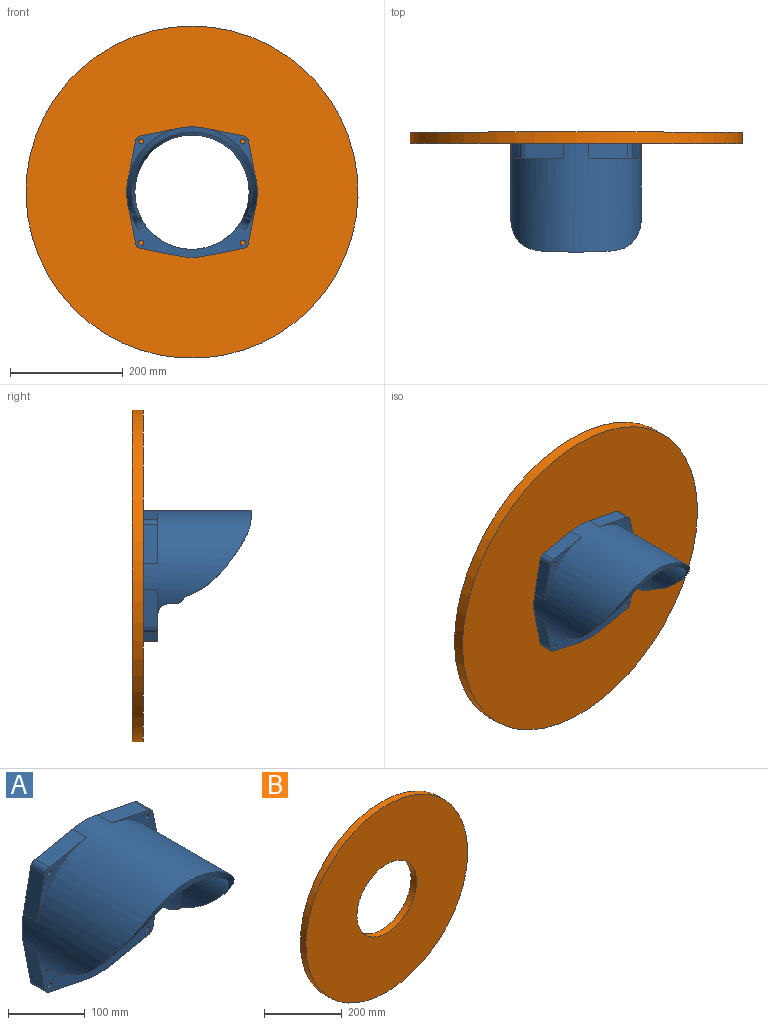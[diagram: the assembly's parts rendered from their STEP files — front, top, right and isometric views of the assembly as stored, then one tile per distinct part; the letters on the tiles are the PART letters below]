
ASSEMBLY  parts=2 mates=1
PART A: 34 faces, bbox 232x193x232 mm
  f0: extruded ~232x154.46mm, area 4830.5mm2, adj f1,f2,f30,f31
  f1: cylinder r=107mm len=214mm, axis (0,1,0), area 37338.6mm2, adj f0,f29,f30,f31
  f2: cylinder r=116mm len=232mm, axis (0,1,0), area 66384.4mm2, adj f0,f3,f4,f5,f11,f12,f14,f15
  f3: plane 90.81x90.81mm, normal (0,-1,0), area 978.9mm2, adj f2,f15,f16,f17,f21
  f4: plane 90.81x90.81mm, normal (0,-1,0), area 978.9mm2, adj f2,f12,f13,f14,f20
  f5: plane 227.43x93.09mm, normal (0,-1,0), area 4952.2mm2, adj f2,f6,f7,f8,f9,f10,f11,f18
  f6: cylinder r=10mm len=26mm, axis (0,1,0), area 305mm2, adj f5,f7,f18,f19
  f7: plane 69.07x26mm, normal (-0.2,0,-0.98), area 1831.8mm2, adj f5,f6,f8,f19
  f8: cylinder r=116mm len=45.81mm, axis (0,1,0), area 1199mm2, adj f5,f7,f9,f19
  f9: plane 69.07x26mm, normal (0.2,0,-0.98), area 1831.8mm2, adj f5,f8,f10,f19
  f10: cylinder r=10mm len=26mm, axis (0,1,0), area 305mm2, adj f5,f9,f11,f19
  f11: plane 69.07x26mm, normal (0.98,0,-0.2), area 1831.8mm2, adj f2,f5,f10,f19
  f12: plane 69.07x26mm, normal (0.98,0,0.2), area 1831.8mm2, adj f2,f4,f13,f19
  f13: cylinder r=10mm len=26mm, axis (0,1,0), area 305mm2, adj f4,f12,f14,f19
  f14: plane 69.07x26mm, normal (0.2,0,0.98), area 1831.8mm2, adj f2,f4,f13,f19
  f15: plane 69.07x26mm, normal (-0.2,0,0.98), area 1831.8mm2, adj f2,f3,f16,f19
  f16: cylinder r=10mm len=26mm, axis (0,1,0), area 305mm2, adj f3,f15,f17,f19
  f17: plane 69.07x26mm, normal (-0.98,0,0.2), area 1831.8mm2, adj f2,f3,f16,f19
  f18: plane 69.07x26mm, normal (-0.98,0,-0.2), area 1831.8mm2, adj f2,f5,f6,f19
  f19: plane 232x232mm, normal (0,1,0), area 9034.5mm2, adj f2,f6,f7,f8,f9,f10,f11,f12
  f20: cylinder r=4.5mm len=26mm, axis (0,1,0), area 735.1mm2, adj f4,f19
  f21: cylinder r=4.5mm len=26mm, axis (0,1,0), area 735.1mm2, adj f3,f19
  f22: cylinder r=4.5mm len=26mm, axis (0,1,0), area 735.1mm2, adj f5,f19
  f23: cylinder r=4.5mm len=26mm, axis (0,1,0), area 735.1mm2, adj f5,f19
  f24: cylinder r=108.75mm len=217.5mm, axis (0,1,0), area 9566.1mm2, adj f19,f25
  f25: cone r=108.75mm half-angle=50.4deg, axis (0,1,0), area 6216mm2, adj f24,f26
  f26: cylinder r=101.5mm len=203mm, axis (0,1,0), area 3826.5mm2, adj f5,f25,f29
  f27: plane 11.02x11mm, normal (0.42,0,-0.91), area 126.7mm2, adj f2,f29,f31,f33
  f28: plane 11.02x11mm, normal (-0.42,0,-0.91), area 126.7mm2, adj f2,f29,f30,f32
  f29: cone r=107mm half-angle=6.7deg, axis (0,-1,0), area 19865.4mm2, adj f1,f26,f27,f28,f30,f31,f32,f33
  f30: cylinder r=16mm len=19.1mm, axis (-0.91,0,0.42), area 185.1mm2, adj f0,f1,f2,f28,f29
  f31: cylinder r=16mm len=19.1mm, axis (-0.91,0,-0.42), area 185.1mm2, adj f0,f1,f2,f27,f29
  f32: cylinder r=20mm len=25.1mm, axis (-0.91,0,0.42), area 430.6mm2, adj f2,f5,f28,f29
  f33: cylinder r=20mm len=25.1mm, axis (-0.91,0,-0.42), area 430.6mm2, adj f2,f5,f27,f29
PART B: 4 faces, bbox 590x20x590 mm
  f0: cylinder r=108.75mm len=217.5mm, axis (0,1,0), area 13665.9mm2, adj f2,f3
  f1: cylinder r=295mm len=590mm, axis (0,1,0), area 37070.8mm2, adj f2,f3
  f2: plane 590x590mm, normal (0,-1,0), area 236242.9mm2, adj f0,f1
  f3: plane 590x590mm, normal (0,1,0), area 236242.9mm2, adj f0,f1
PLACE A t=(0,-20,0)mm
PLACE B rot(axis=(1,0,0),180deg) t=(0,-20,0)mm
MATE fastened B.f0 <-> A.f24  axis (0,-1,0) through (0,-20,0)mm
